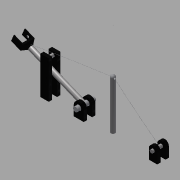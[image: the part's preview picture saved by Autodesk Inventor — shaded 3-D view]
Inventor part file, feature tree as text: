
AUTODESK INVENTOR PART (.ipt)
format: ipt  version: 2015 (Build 190159000, 159)  size: 310,784 bytes
history: native  units: in
note: dims shown in document units (in); Inventor stores cm internally (conversion verified against a paired STEP export)
features: sketch x17, extrude x13, plane x8, mirror x3, sweep x2, other x2, loft x1, thread x1, fillet x1
ambient origin geometry x8: Origin, YZ Plane, XZ Plane, XY Plane, X Axis, Y Axis, Z Axis, Center Point
bodies: Solid1 (feature_tree)
feature tree (48):
  extrude  "Extrusion1"  Depth=0.2362in
  plane  "Work Plane1"
  mirror  "Mirror1"
  plane  "Work Plane2"
  extrude  "Extrusion2"  Depth=0.1181in
  plane  "Work Plane8"
  extrude  "Extrusion3"  Depth=0.0591in
  plane  "Work Plane5"
  extrude  "Extrusion4"  Depth=0.1102in
  loft  "Loft1"
  extrude  "Extrusion5"  Depth=0.0787in
  extrude  "Extrusion6"  Depth=0.0394in
  thread  "Thread1"  [1 undecoded]
  extrude  "Extrusion7"  TaperAngle=0.0deg  [1 undecoded]
  mirror  "Mirror2"
  extrude  "Extrusion8"  Depth=0.0197in
  plane  "Work Plane9"
  extrude  "Extrusion9"  Depth=0.0591in
  plane  "Work Plane10"
  extrude  "Extrusion10"  Depth=0.3937in TaperAngle=0.0deg
  fillet  "Fillet1"  Radius=0.1969in
  extrude  "Extrusion11"  Depth=0.0787in
  mirror  "Mirror3"
  extrude  "Extrusion12"  Depth=0.0984in
  sketch  "Sketch21"  dims[d41=0.2756in d42=0.0in d45=0.0984in]
  plane  "Work Plane11"
  sweep  "Sweep1"
  extrude  "Extrusion13"  Depth=0.0591in
  sketch  "Sketch24"  dims[d51=0.3937in d52=0.0in d53=0.0492in]
  plane  "Work Plane12"
  sweep  "Sweep2"
  sketch  "Sketch1"  dims[d0=0.5906in d1=0.2362in]
  sketch  "Sketch2"  dims[d2=0.2362in d3=0.1181in]
  sketch  "Sketch6"  dims[d4=0.0787in d5=0.0in d6=0.0591in]
  sketch  "Sketch8"  dims[d7=0.0787in d8=0.1102in]
  other  "Edges1"
  other  "Edges2"
  sketch  "Sketch9"  dims[d9=0.4331in d10=0.0in d13=0.1102in]
  sketch  "Sketch10"  dims[d14=1.378in d15=0.0in d18=0.0787in]
  sketch  "Sketch13"  dims[d19=0.2756in d20=0.1575in d21=0.0394in d22=0.0in]
  sketch  "Sketch14"  dims[d23=0.0in d24=90.0deg d25=0.0in d26=90.0deg]
  sketch  "Sketch17"  dims[d27=0.0197in d28=0.0197in]
  sketch  "Sketch18"  dims[d29=0.1969in d30=0.0in d31=0.0591in]
  sketch  "Sketch19"  dims[d32=0.1969in d33=0.0in d34=0.3937in d35=0.0in d37=0.1969in]
  sketch  "Sketch20"  dims[d38=0.0787in d39=0.0in d40=0.0787in]
  sketch  "Sketch22"  dims[d46=1.1811in d47=0.0in d48=0.7874in]
  sketch  "Sketch23"  dims[d49=0.0591in d50=0.0472in]
  sketch  "Sketch25"  dims[d54=1.7717in d55=0.3543in d56=0.1969in d57=0.2362in d58=0.1969in d59=0.0787in d60=0.0in d61=0.0787in d62=0.315in d63=0.0394in d64=0.0in d65=0.0in d66=0.0039in d67=0.0in d68=0.0in d69=0.0394in d70=0.0in d71=0.0039in d72=0.0in d73=0.0in]
note: 2 required parameter values undecoded (feature->parameter linkage not recoverable at this tier; creation-order binding heuristic only, values carry confidence <= 0.55)
